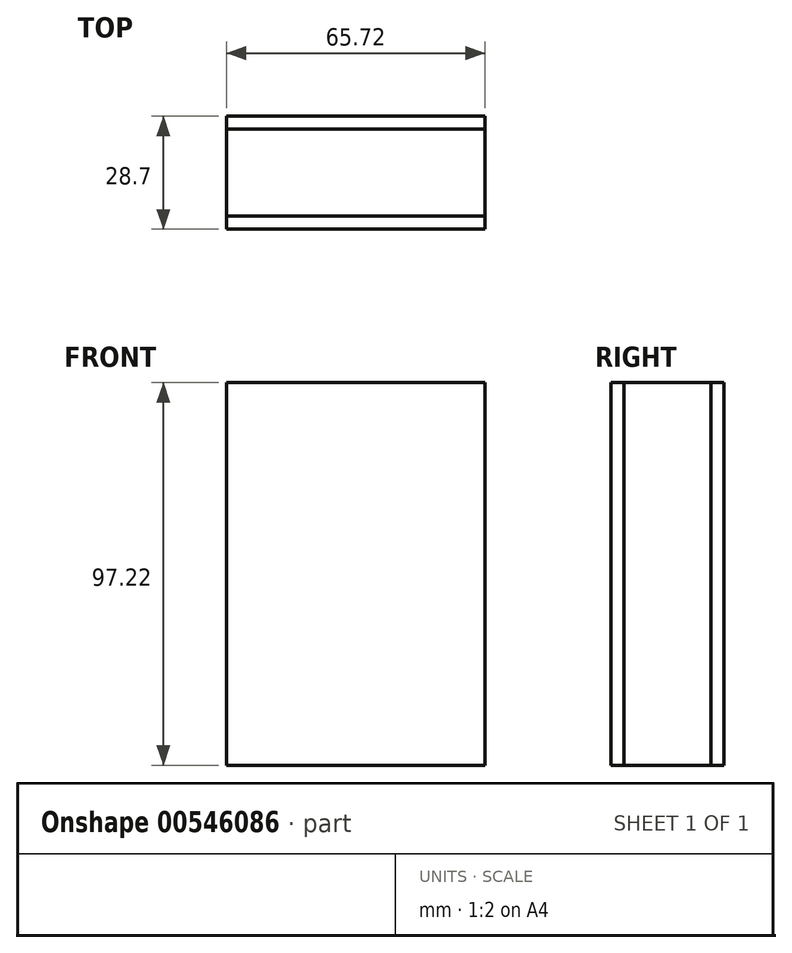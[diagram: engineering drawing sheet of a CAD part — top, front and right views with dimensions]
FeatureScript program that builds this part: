
annotation { "Feature Type Name" : "Feature", "Feature Type Description" : "" }
export const myFeature = defineFeature(function(context is Context, id is Id, definition is map)
    precondition{}
    {
        {
            var Q0;
            Q0=qCreatedBy(makeId("Front.planeOp"),FACE);
            var sketch = newSketch(context, id + "F0", { "sketchPlane" : qUnion([Q0])});
            skLineSegment(sketch, "E0.bottom", {"start": v(-29.13, 45.79) * mm, "end": v(36.6, 45.79) * mm});
            skLineSegment(sketch, "E0.top", {"start": v(-29.13, -51.43) * mm, "end": v(36.6, -51.43) * mm});
            skLineSegment(sketch, "E0.left", {"start": v(-29.13, 45.79) * mm, "end": v(-29.13, -51.43) * mm});
            skLineSegment(sketch, "E0.right", {"start": v(36.6, 45.79) * mm, "end": v(36.6, -51.43) * mm});
            skLineSegment(sketch, "E1.bottom", {"start": v(36.6, 45.79) * mm, "end": v(-29.13, 45.79) * mm});
            skLineSegment(sketch, "E1.top", {"start": v(36.6, 53.07) * mm, "end": v(-29.13, 53.07) * mm});
            skLineSegment(sketch, "E1.left", {"start": v(36.6, 45.79) * mm, "end": v(36.6, 53.07) * mm});
            skLineSegment(sketch, "E1.right", {"start": v(-29.13, 45.79) * mm, "end": v(-29.13, 53.07) * mm});
            skSolve(sketch);
        }
        {
            var Q0;
            Q0=makeQuery(id+"F0.imprint","IMPRINT",FACE,{"disambiguationData":[TD([[makeQuery(id+"F0.imprint","IMPRINT",EDGE,{"derivedFrom":sQuery(id+"F0.wireOp",EDGE,"E0.top")}),1.0]])]});
            extrude(context, id + "F1", {"entities" : qUnion([Q0]), "depth" : 25.4 * mm, "offsetDistance" : 25.4 * mm});
        }
        {
            var Q0;
            Q0=makeQuery(id+"F1.opExtrude","CAP_FACE",FACE,{"disambiguationData":[OSD([sQuery(id+"F0.wireOp",EDGE,"E0.top"),sQuery(id+"F0.wireOp",EDGE,"E0.left"),sQuery(id+"F0.wireOp",EDGE,"E0.right"),sQuery(id+"F0.wireOp",EDGE,"E1.bottom")])],"isStart":false});
            var Q1;
            Q1=makeQuery(id+"F1.opExtrude","SWEPT_FACE",FACE,{"disambiguationData":[OSD([sQuery(id+"F0.wireOp",EDGE,"E1.bottom")])]});
            var Q2;
            Q2=makeQuery(id+"F1.opExtrude","CAP_FACE",FACE,{"disambiguationData":[OSD([sQuery(id+"F0.wireOp",EDGE,"E0.top"),sQuery(id+"F0.wireOp",EDGE,"E0.left"),sQuery(id+"F0.wireOp",EDGE,"E0.right"),sQuery(id+"F0.wireOp",EDGE,"E1.bottom")])],"isStart":true});
            extrude(context, id + "F2", {"entities" : qUnion([Q0, Q1, Q2]), "depth" : 3.3 * mm, "offsetDistance" : 25.4 * mm});
        }
    });
